# Revit family: Building-ConnessioniIEC309-GEWISS-67IB-PRESE-INTERBLOCCATE_IP67_CON_FONDO_24V
name_source: partatom
category: Apparecchi elettrici
units: mm (PartAtom-declared; Revit-internal decimal feet)

## family parameters
Condiviso = Sì
Host = Superficie
Mantenere orientamento annotazione = Sì
Punto di calcolo locali = Sì
Quota connettore circolare = Usa diametro
Taglio con vuoti quando caricato = Sì
Tipo di parte = Normale

## types (1)
- GW66259N -  PR.BL.C.F.2P.160VA TRASF.230/24V IP67
    Catalogo = BUILDING
    Codice Electrocod = 2222
    Colore: = Viola
    Con fondo = Si
    Corpo presa = Light Blue
    Corrente nominale (A) = 16
    Descrizione = PR.BL.C.F.2P.160VA TRASF.230/24V IP67
    Frequenza = 50 Hz
    Glow wire test: = 850 °C (Presa IB) - 650 °C (Cassetta di fondo)
    Grado di protezione = IP67
    IDF = 39939390-56cf-44cd-acec-389131e572e6
    IDT = 6291d3a6c8ec4742af7995575e50af9c
    Immagine tipo = <Nessuno>
    Modello = GW66259N
    N. poli = 2P
    Potenza nominale = 160VA
    Produttore = GEWISS S.p.A.
    Prospetto di default = 1219 mm
    Protezione = Trasformatore di sicurezza
    Resistenza agli urti = IK08
    SEO = Presa
    Scheda Tecnica = https://www.gewiss.com
    Simbolo presa = PRESAINDSTAGNA : 3P
    Struttura = Grigio RAL - 7035
    T1 = 230V
    T2 = 24V
    Temperatura di utilizzo = -25 +40 °C
    Tensione di uscita = 20-25 V
    Termopressione con biglia = 125 °C (Presa IB) - 80 °C (Cassetta di fondo)
    Tipologia = Verticale
    URL = https://www.gewiss.com
    Versione file RFA = 21.8
    giallo = 0 mm  [stored 0 ft]
    presa = Grigio RAL - 7035

note: [stored X ft] marks values corroborated as IEEE doubles in the binary element streams (Revit-internal decimal feet)

## geometry (parser evidence)
native form markers: Sweep x5
no freeform markers — native parametric forms only
